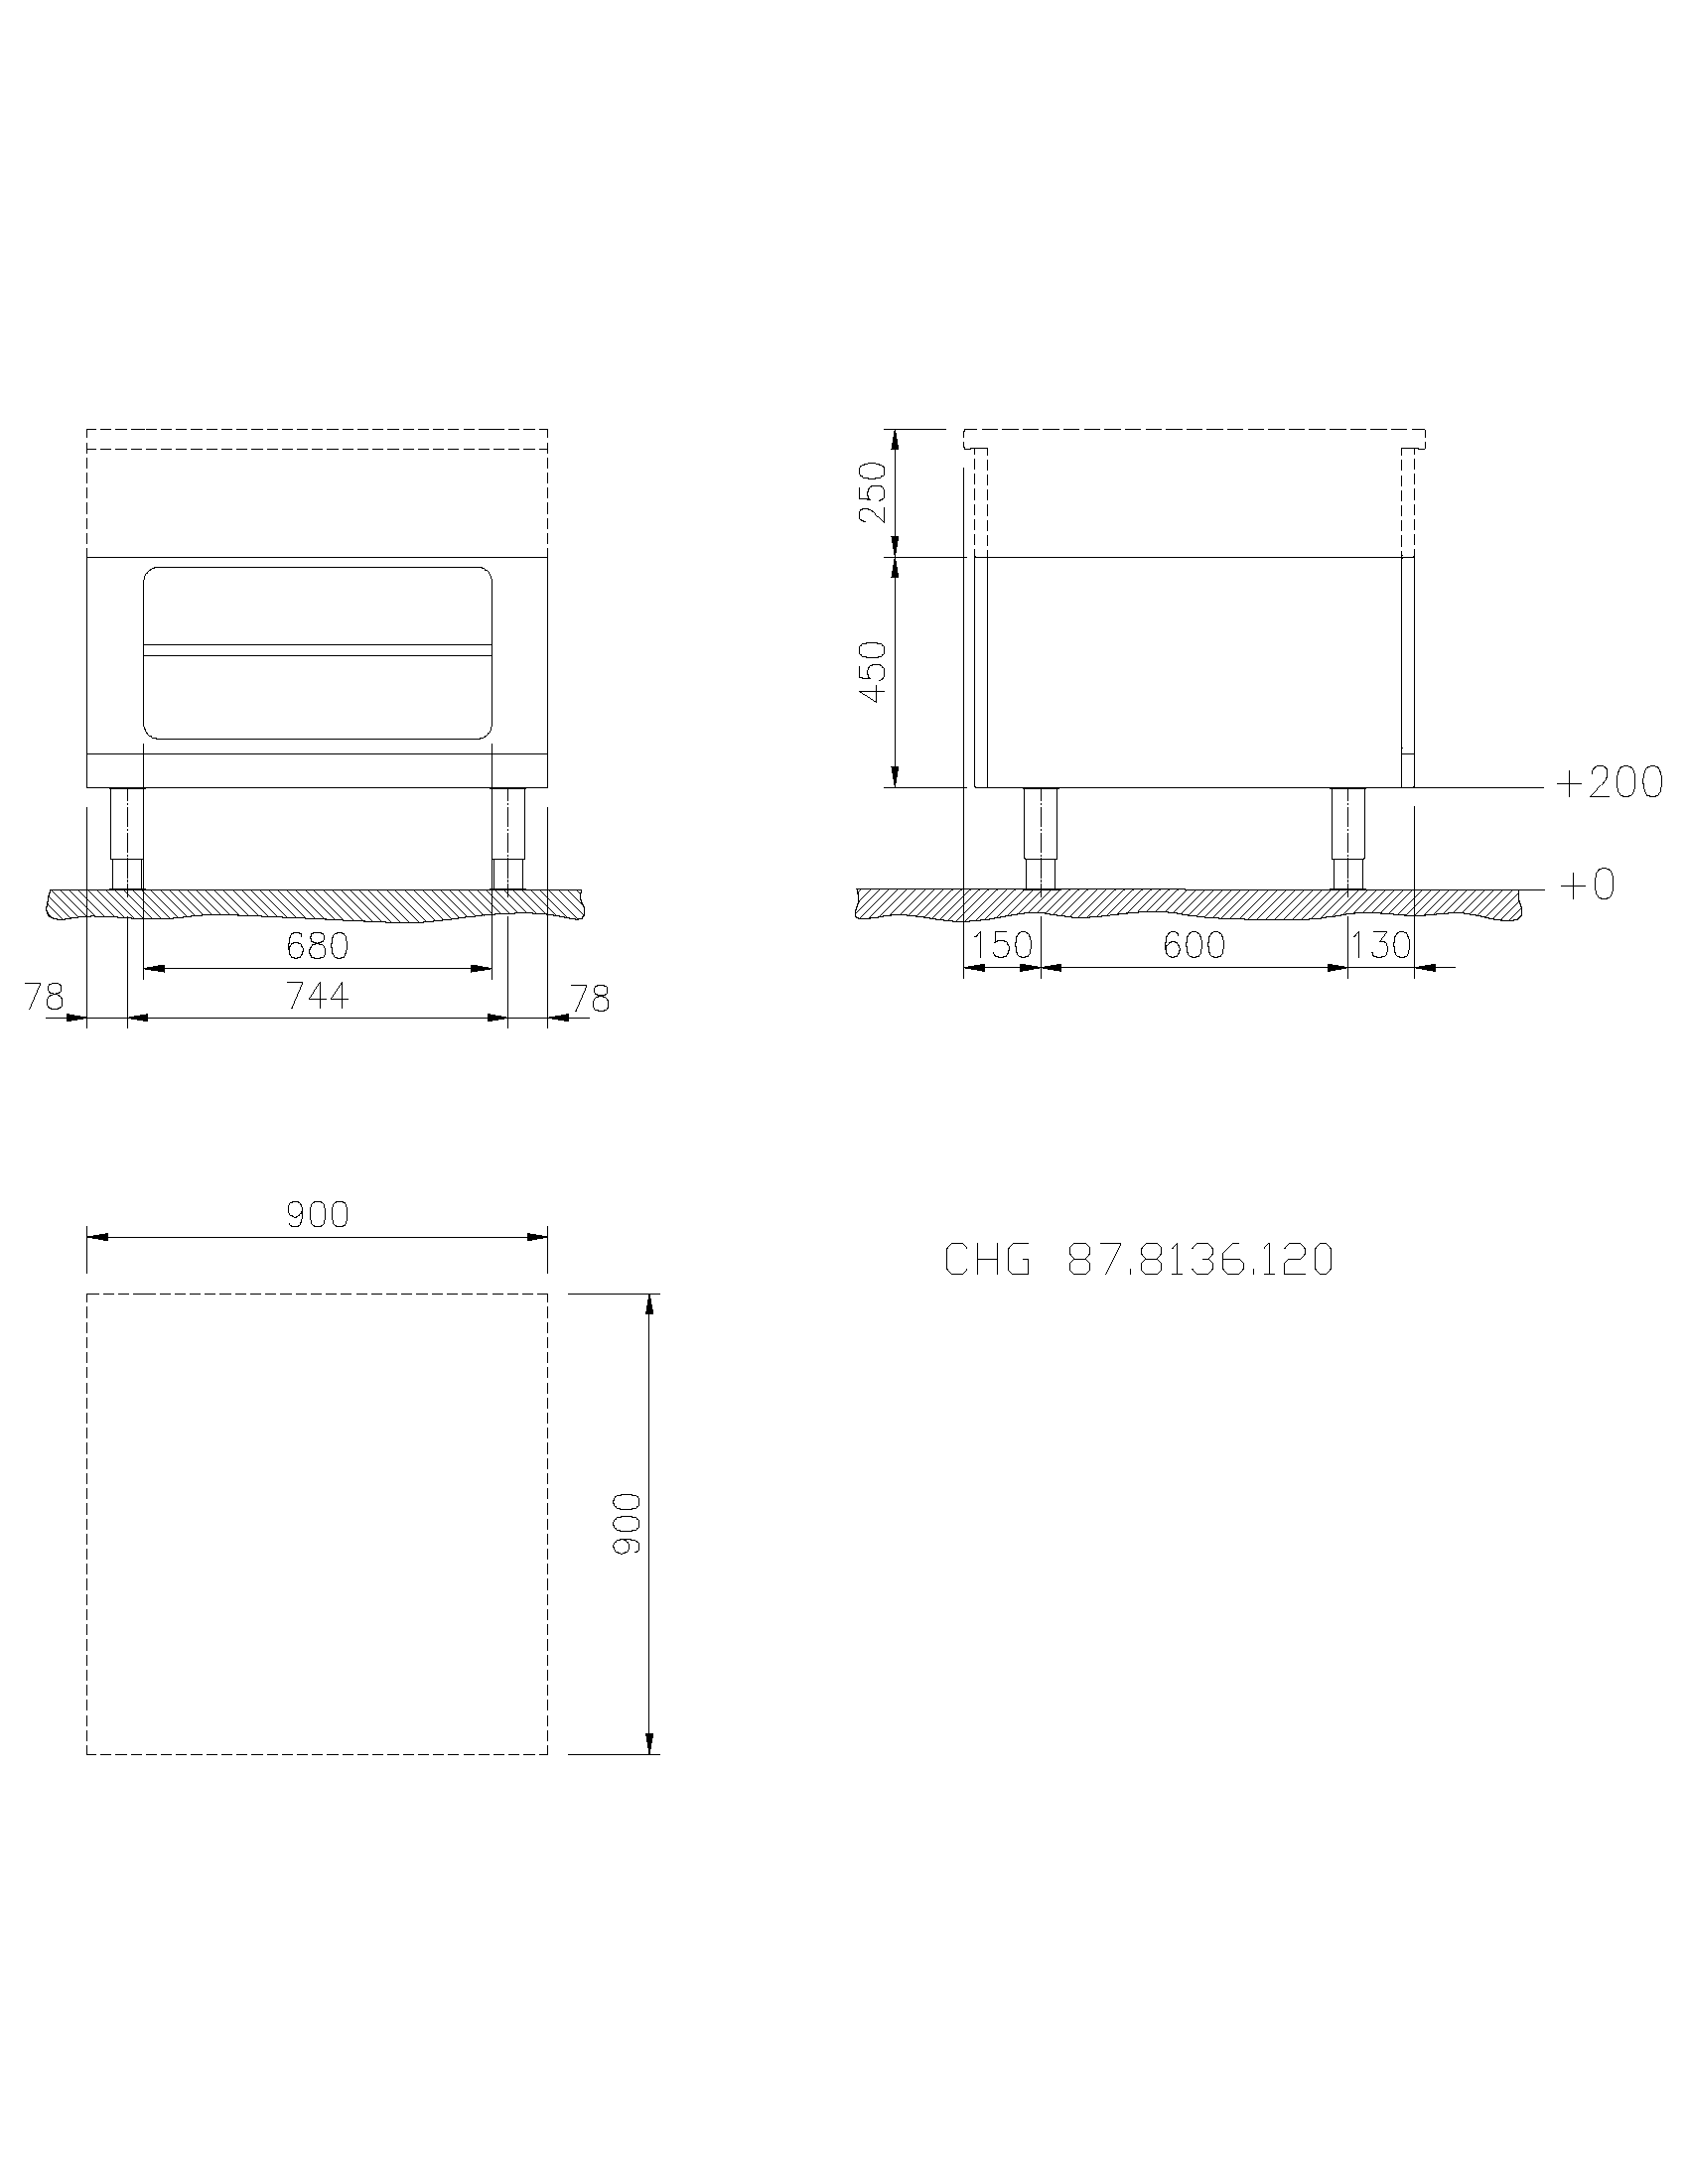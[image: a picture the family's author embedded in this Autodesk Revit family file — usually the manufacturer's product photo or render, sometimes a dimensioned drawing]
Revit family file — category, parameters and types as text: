
# Revit family: QF_ELECTROLUXPROFESSIONAL_589821_MCBBEAH1DM
name_source: partatom
category: Attrezzature speciali
units: mm (PartAtom-declared; Revit-internal decimal feet)

## family parameters
Basato su piano di lavoro = No
Condiviso = No
Punto di calcolo locali = No
Quota connettore circolare = Usa diametro
Sempre verticale = Sì
Taglio con vuoti quando caricato = No
Tipo di parte = Normale

## types (1)
- Standard
    Accessory = Sì
    Cold Water Size = 1"
    Compressed Air Pressure = 0.00 psi
    Compressed Air Size = 0"
    Compressed Air Volume = 0 GPM
    Condensate Return Size = 0"
    Cycle = 50 Hz
    Depth Actual = 900 mm  [stored 2.95276 ft]
    Descrizione = BAINM,2/1GN,TAP(B)1S,800X900X700 MARINE
    Direct Waste Size = 1"
    Gas Input Pressure = 0.0
    Gas KW = 0
    Gas Size = 0"
    HP = 4 HP
    Height Actual = 700 mm  [stored 2.29659 ft]
    Hot Water Size = 1"
    Item Number = 589821
    Length Actual = 800 mm  [stored 2.62467 ft]
    Modello = MCBBEAH1DM
    Phase = 3
    Produttore = Electrolux Professional
    Prospetto di default = 0 mm  [stored 0 ft]
    Refrigerant Compressor Remote = Sì
    Refrigeration Liquid Line Size = 0 mm  [stored 0 ft]
    Refrigeration Suction Line Size = 0 mm  [stored 0 ft]
    Steam Consumption per Hour = 0
    Steam Supply Maximum Pressure = 0.00 psi
    Steam Supply Minimum Pressure = 0.00 psi
    Steam Supply Size = 0"
    URL = https://www.electroluxprofessional.com
    URL Manufacturer = https://www.electroluxprofessional.com
    Volts = 440 V
    Watts = 3000 W
    Weight = 57.00 kg

note: source unit labels omitted for Gas Input Pressure — the stored unit's dimension contradicts the parameter name (converter mislabeling)

note: [stored X ft] marks values corroborated as IEEE doubles in the binary element streams (Revit-internal decimal feet)

## geometry (parser evidence)
native form markers: Blend x1, Sweep x10
no freeform markers — native parametric forms only
